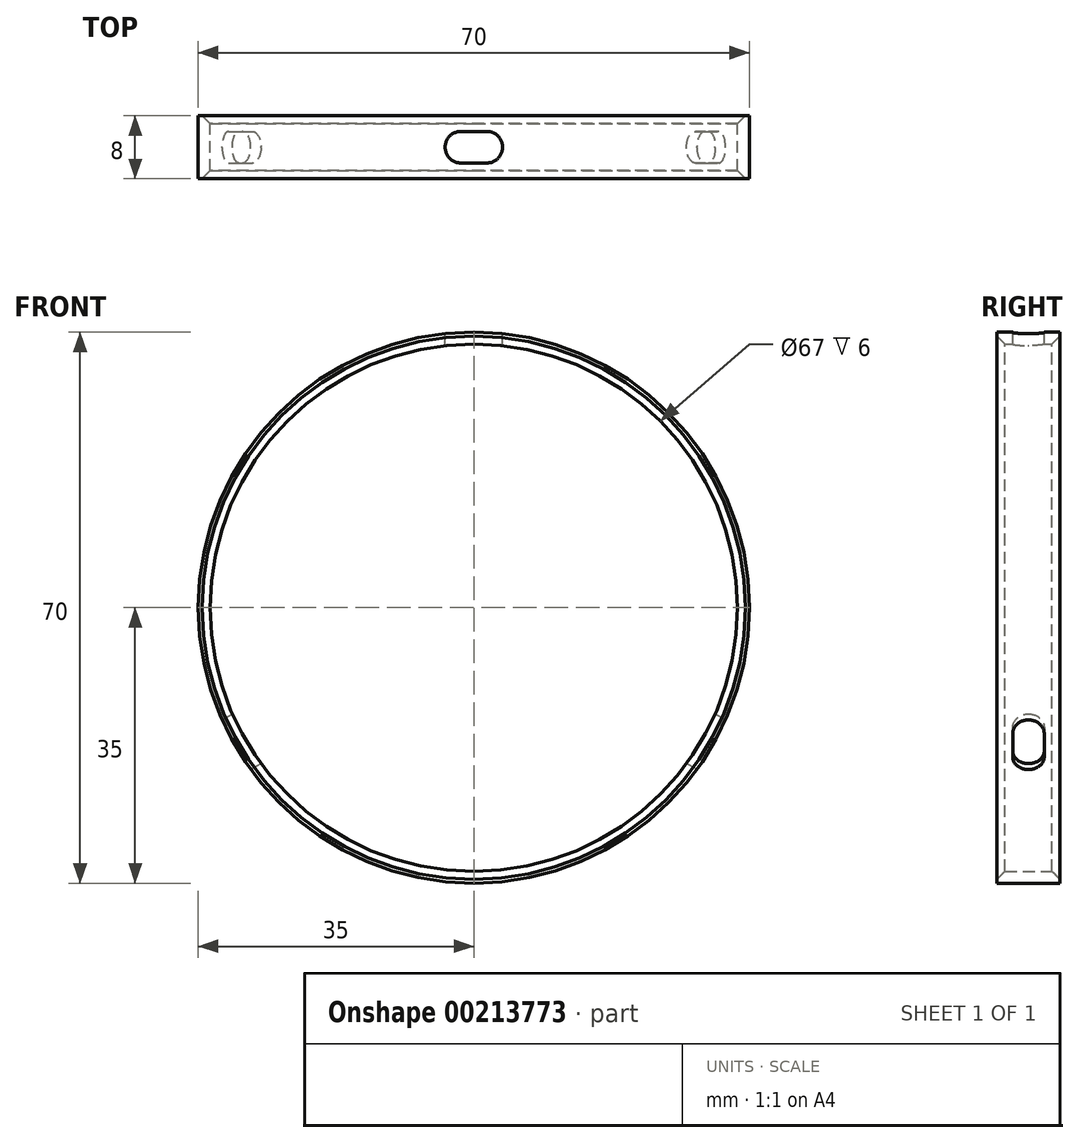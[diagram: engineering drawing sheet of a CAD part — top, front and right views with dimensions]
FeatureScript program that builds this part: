
annotation { "Feature Type Name" : "Feature", "Feature Type Description" : "" }
export const myFeature = defineFeature(function(context is Context, id is Id, definition is map)
    precondition{}
    {
        {
            var Q0;
            Q0=qCreatedBy(makeId("Front.planeOp"),FACE);
            var sketch = newSketch(context, id + "F0", { "sketchPlane" : qUnion([Q0])});
            skCircle(sketch, "E0", {"center": v(0, 0) * mm, "radius": 33.5 * mm});
            skCircle(sketch, "E1.0", {"center": v(0, 0) * mm, "radius": 35 * mm});
            skLineSegment(sketch, "E2.bottom", {"start": v(3.63, 34.81) * mm, "end": v(-3.63, 34.81) * mm, "construction": true});
            skLineSegment(sketch, "E2.top", {"start": v(3.63, 36.97) * mm, "end": v(-3.63, 36.97) * mm});
            skLineSegment(sketch, "E2.left", {"start": v(3.63, 34.81) * mm, "end": v(3.63, 36.97) * mm});
            skLineSegment(sketch, "E2.right", {"start": v(-3.63, 34.81) * mm, "end": v(-3.63, 36.97) * mm});
            skPoint(sketch, "E2.middle", {"position": v(0, 35.89) * mm});
            skLineSegment(sketch, "E3.1.0", {"start": v(-28.33, -20.55) * mm, "end": v(-30.2, -21.63) * mm});
            skLineSegment(sketch, "E3.1.1", {"start": v(-31.96, -14.26) * mm, "end": v(-33.83, -15.34) * mm});
            skLineSegment(sketch, "E3.1.2", {"start": v(-33.83, -15.34) * mm, "end": v(-30.2, -21.63) * mm});
            skLineSegment(sketch, "E3.1.3", {"start": v(-31.96, -14.26) * mm, "end": v(-28.33, -20.55) * mm, "construction": true});
            skLineSegment(sketch, "E3.2.0", {"start": v(31.96, -14.26) * mm, "end": v(33.83, -15.34) * mm});
            skLineSegment(sketch, "E3.2.1", {"start": v(28.33, -20.55) * mm, "end": v(30.2, -21.63) * mm});
            skLineSegment(sketch, "E3.2.2", {"start": v(30.2, -21.63) * mm, "end": v(33.83, -15.34) * mm});
            skLineSegment(sketch, "E3.2.3", {"start": v(28.33, -20.55) * mm, "end": v(31.96, -14.26) * mm, "construction": true});
            skLineSegment(sketch, "E4", {"start": v(0, 0) * mm, "end": v(24.75, 24.75) * mm, "construction": true});
            skLineSegment(sketch, "E5", {"start": v(0, 0) * mm, "end": v(-24.75, 24.75) * mm, "construction": true});
            skLineSegment(sketch, "E6.MirrorCS", {"start": v(0, 0) * mm, "end": v(24.75, -24.75) * mm, "construction": true});
            skLineSegment(sketch, "E7.MirrorCS", {"start": v(0, 0) * mm, "end": v(-24.75, -24.75) * mm, "construction": true});
            skLineSegment(sketch, "E8.0", {"start": v(-0.14, 0.14) * mm, "end": v(0, 0.28) * mm});
            skLineSegment(sketch, "E9.MirrorCS", {"start": v(0.14, -0.14) * mm, "end": v(0.28, 0) * mm});
            skLineSegment(sketch, "E10.MirrorCS", {"start": v(0.14, 0.14) * mm, "end": v(0, 0.28) * mm});
            skLineSegment(sketch, "E11.MirrorCS", {"start": v(-0.14, -0.14) * mm, "end": v(-0.28, 0) * mm});
            skLineSegment(sketch, "E12.MirrorCS", {"start": v(0.14, 0.14) * mm, "end": v(0.28, 0) * mm});
            skLineSegment(sketch, "E13.MirrorCS", {"start": v(-0.14, -0.14) * mm, "end": v(0, -0.28) * mm});
            skLineSegment(sketch, "E14.MirrorCS", {"start": v(0.14, -0.14) * mm, "end": v(0, -0.28) * mm});
            skLineSegment(sketch, "E15.MirrorCS", {"start": v(-0.14, 0.14) * mm, "end": v(-0.28, 0) * mm});
            skLineSegment(sketch, "E16.trimOffspring", {"start": v(-7.2, -7.48) * mm, "end": v(-23.55, -23.83) * mm, "construction": true});
            skLineSegment(sketch, "E17.trimOffspring", {"start": v(-7.48, -7.2) * mm, "end": v(-23.83, -23.55) * mm, "construction": true});
            skLineSegment(sketch, "E18.trimOffspring", {"start": v(-7.48, 7.2) * mm, "end": v(-23.83, 23.55) * mm, "construction": true});
            skLineSegment(sketch, "E19.trimOffspring", {"start": v(-7.2, 7.48) * mm, "end": v(-23.55, 23.83) * mm, "construction": true});
            skLineSegment(sketch, "E20.trimOffspring", {"start": v(7.2, 7.48) * mm, "end": v(23.55, 23.83) * mm, "construction": true});
            skLineSegment(sketch, "E21.trimOffspring", {"start": v(7.48, 7.2) * mm, "end": v(23.83, 23.55) * mm, "construction": true});
            skLineSegment(sketch, "E22.trimOffspring", {"start": v(7.2, -7.48) * mm, "end": v(23.55, -23.83) * mm, "construction": true});
            skLineSegment(sketch, "E23.trimOffspring", {"start": v(7.48, -7.2) * mm, "end": v(23.83, -23.55) * mm, "construction": true});
            skLineSegment(sketch, "E24", {"start": v(-3.63, 34.81) * mm, "end": v(-3.63, 31.7) * mm});
            skLineSegment(sketch, "E25", {"start": v(-3.63, 31.7) * mm, "end": v(3.63, 31.7) * mm});
            skLineSegment(sketch, "E26", {"start": v(3.63, 31.7) * mm, "end": v(3.63, 34.81) * mm});
            skLineSegment(sketch, "E27", {"start": v(31.96, -14.26) * mm, "end": v(7.27, 0) * mm});
            skLineSegment(sketch, "E28", {"start": v(28.33, -20.55) * mm, "end": v(3.35, -6.13) * mm});
            skLineSegment(sketch, "E29", {"start": v(3.35, -6.13) * mm, "end": v(7.27, 0) * mm});
            skLineSegment(sketch, "E30", {"start": v(-28.33, -20.55) * mm, "end": v(-3.28, -6.1) * mm});
            skLineSegment(sketch, "E31", {"start": v(-31.96, -14.26) * mm, "end": v(-6.86, 0.24) * mm});
            skLineSegment(sketch, "E32", {"start": v(-6.86, 0.24) * mm, "end": v(-3.28, -6.1) * mm});
            skLineSegment(sketch, "E33", {"start": v(0, -0.28) * mm, "end": v(0, 35) * mm, "construction": true});
            skLineSegment(sketch, "E34", {"start": v(0.28, 0) * mm, "end": v(-20.96, 28.03) * mm});
            skLineSegment(sketch, "E35.MirrorCS", {"start": v(-0.28, 0) * mm, "end": v(20.96, 28.03) * mm});
            skSolve(sketch);
        }
        {
            var Q0;
            Q0=makeQuery(id+"F0.imprint","IMPRINT",FACE,{"disambiguationData":[TD([[makeQuery(id+"F0.imprint","IMPRINT",EDGE,{"derivedFrom":sQuery(id+"F0.wireOp",EDGE,"E0")}),-1.0]])]});
            var Q1;
            {var subQ2=sQuery(id+"F0.wireOp",EDGE,"E16.trimOffspring");var subQ7=sQuery(id+"F0.wireOp",EDGE,"E0");var subQ9=makeQuery(id+"F0.imprint","INTERSECT",VERTEX,{"derivedFrom":[subQ7,subQ2]});Q1=makeQuery(id+"F0.imprint","IMPRINT",FACE,{"disambiguationData":[TD([[makeQuery(id+"F0.imprint","IMPRINT",EDGE,{"disambiguationData":[TD([[subQ9,-1.0]])],"derivedFrom":subQ7}),-1.0]])]});}
            var Q2;
            {var subQ5=sQuery(id+"F0.wireOp",EDGE,"E21.trimOffspring");var subQ7=sQuery(id+"F0.wireOp",EDGE,"E0");var subQ8=makeQuery(id+"F0.imprint","INTERSECT",VERTEX,{"derivedFrom":[subQ7,subQ5]});Q2=makeQuery(id+"F0.imprint","IMPRINT",FACE,{"disambiguationData":[TD([[makeQuery(id+"F0.imprint","IMPRINT",EDGE,{"disambiguationData":[TD([[subQ8,1.0]])],"derivedFrom":subQ7}),-1.0]])]});}
            var Q3;
            {var subQ2=sQuery(id+"F0.wireOp",EDGE,"E19.trimOffspring");var subQ7=sQuery(id+"F0.wireOp",EDGE,"E0");var subQ8=makeQuery(id+"F0.imprint","INTERSECT",VERTEX,{"derivedFrom":[subQ7,subQ2]});Q3=makeQuery(id+"F0.imprint","IMPRINT",FACE,{"disambiguationData":[TD([[makeQuery(id+"F0.imprint","IMPRINT",EDGE,{"disambiguationData":[TD([[subQ8,1.0]])],"derivedFrom":subQ7}),-1.0]])]});}
            var Q4;
            {var subQ5=sQuery(id+"F0.wireOp",EDGE,"E17.trimOffspring");var subQ6=sQuery(id+"F0.wireOp",EDGE,"E0");var subQ7=makeQuery(id+"F0.imprint","INTERSECT",VERTEX,{"derivedFrom":[subQ6,subQ5]});Q4=makeQuery(id+"F0.imprint","IMPRINT",FACE,{"disambiguationData":[TD([[makeQuery(id+"F0.imprint","IMPRINT",EDGE,{"disambiguationData":[TD([[subQ7,1.0]])],"derivedFrom":subQ6}),-1.0]])]});}
            extrude(context, id + "F1", {"entities" : qUnion([Q0, Q1, Q2, Q3, Q4]), "depth" : 4 * mm, "hasSecondDirection" : true, "secondDirectionOppositeDirection" : true, "secondDirectionDepth" : 4 * mm});
        }
        {
            var Q0;
            Q0=makeQuery(id+"F1.opExtrude","CAP_EDGE",EDGE,{"disambiguationData":[OSD([sQuery(id+"F0.wireOp",EDGE,"E0")])],"isStart":false});
            var Q1;
            Q1=makeQuery(id+"F1.opExtrude","CAP_EDGE",EDGE,{"disambiguationData":[OSD([sQuery(id+"F0.wireOp",EDGE,"E0")])],"isStart":true});
            chamfer(context, id + "F2", {"entities" : qUnion([Q0, Q1]), "width" : 1 * mm, "tangentPropagation" : true});
        }
        {
            var Q0;
            Q0=qCreatedBy(makeId("Top.planeOp"),FACE);
            var sketch = newSketch(context, id + "F3", { "sketchPlane" : qUnion([Q0])});
            skCircle(sketch, "E36", {"center": v(0, 0) * mm, "radius": 0.15 * mm});
            skCircle(sketch, "E37.1.0.0", {"center": v(0, -0.6) * mm, "radius": 0.15 * mm});
            skCircle(sketch, "E37.2.0.0", {"center": v(0, -1.2) * mm, "radius": 0.15 * mm});
            skCircle(sketch, "E37.3.0.0", {"center": v(0, -1.8) * mm, "radius": 0.15 * mm});
            skCircle(sketch, "E37.4.0.0", {"center": v(0, -2.4) * mm, "radius": 0.15 * mm});
            skCircle(sketch, "E37.5.0.0", {"center": v(0, -3) * mm, "radius": 0.15 * mm});
            skCircle(sketch, "E37.6.0.0", {"center": v(0, -3.6) * mm, "radius": 0.15 * mm});
            skLineSegment(sketch, "E37.direction1", {"start": v(0, 0) * mm, "end": v(0, -0.6) * mm, "construction": true});
            skCircle(sketch, "E38.MirrorC", {"center": v(0, 0.6) * mm, "radius": 0.15 * mm});
            skCircle(sketch, "E39.MirrorC", {"center": v(0, 1.2) * mm, "radius": 0.15 * mm});
            skCircle(sketch, "E40.MirrorC", {"center": v(0, 1.8) * mm, "radius": 0.15 * mm});
            skCircle(sketch, "E41.MirrorC", {"center": v(0, 2.4) * mm, "radius": 0.15 * mm});
            skCircle(sketch, "E42.MirrorC", {"center": v(0, 3) * mm, "radius": 0.15 * mm});
            skCircle(sketch, "E43.MirrorC", {"center": v(0, 3.6) * mm, "radius": 0.15 * mm});
            skSolve(sketch);
        }
        {
            var Q0;
            Q0=makeQuery(id+"F0.imprint","IMPRINT",FACE,{"disambiguationData":[TD([[makeQuery(id+"F0.imprint","IMPRINT",EDGE,{"derivedFrom":sQuery(id+"F0.wireOp",EDGE,"E2.top")}),1.0]])]});
            var Q1;
            {var subQ0=sQuery(id+"F0.wireOp",EDGE,"E24");var subQ1=sQuery(id+"F0.wireOp",EDGE,"E0");var subQ2=makeQuery(id+"F0.imprint","INTERSECT",VERTEX,{"derivedFrom":[subQ1,subQ0]});Q1=makeQuery(id+"F0.imprint","IMPRINT",FACE,{"disambiguationData":[TD([[makeQuery(id+"F0.imprint","IMPRINT",EDGE,{"disambiguationData":[TD([[subQ2,1.0]])],"derivedFrom":subQ1}),-1.0]])]});}
            var Q2;
            {var subQ5=sQuery(id+"F0.wireOp",EDGE,"E25");Q2=makeQuery(id+"F0.imprint","IMPRINT",FACE,{"disambiguationData":[TD([[makeQuery(id+"F0.imprint","IMPRINT",EDGE,{"derivedFrom":subQ5}),1.0]])]});}
            var Q3;
            {var subQ5=sQuery(id+"F0.wireOp",EDGE,"E29");Q3=makeQuery(id+"F0.imprint","IMPRINT",FACE,{"disambiguationData":[TD([[makeQuery(id+"F0.imprint","IMPRINT",EDGE,{"derivedFrom":subQ5}),-1.0]])]});}
            var Q4;
            {var subQ0=sQuery(id+"F0.wireOp",EDGE,"E28");var subQ1=sQuery(id+"F0.wireOp",EDGE,"E0");var subQ2=makeQuery(id+"F0.imprint","INTERSECT",VERTEX,{"derivedFrom":[subQ1,subQ0]});Q4=makeQuery(id+"F0.imprint","IMPRINT",FACE,{"disambiguationData":[TD([[makeQuery(id+"F0.imprint","IMPRINT",EDGE,{"disambiguationData":[TD([[subQ2,-1.0]])],"derivedFrom":subQ1}),-1.0]])]});}
            var Q5;
            {var subQ0=sQuery(id+"F0.wireOp",EDGE,"E3.2.0");Q5=makeQuery(id+"F0.imprint","IMPRINT",FACE,{"disambiguationData":[TD([[makeQuery(id+"F0.imprint","IMPRINT",EDGE,{"derivedFrom":subQ0}),-1.0]])]});}
            var Q6;
            {var subQ5=sQuery(id+"F0.wireOp",EDGE,"E32");Q6=makeQuery(id+"F0.imprint","IMPRINT",FACE,{"disambiguationData":[TD([[makeQuery(id+"F0.imprint","IMPRINT",EDGE,{"derivedFrom":subQ5}),-1.0]])]});}
            var Q7;
            {var subQ0=sQuery(id+"F0.wireOp",EDGE,"E3.1.0");Q7=makeQuery(id+"F0.imprint","IMPRINT",FACE,{"disambiguationData":[TD([[makeQuery(id+"F0.imprint","IMPRINT",EDGE,{"derivedFrom":subQ0}),-1.0]])]});}
            var Q8;
            {var subQ0=sQuery(id+"F0.wireOp",EDGE,"E31");var subQ1=sQuery(id+"F0.wireOp",EDGE,"E0");var subQ2=makeQuery(id+"F0.imprint","INTERSECT",VERTEX,{"derivedFrom":[subQ1,subQ0]});Q8=makeQuery(id+"F0.imprint","IMPRINT",FACE,{"disambiguationData":[TD([[makeQuery(id+"F0.imprint","IMPRINT",EDGE,{"disambiguationData":[TD([[subQ2,-1.0]])],"derivedFrom":subQ1}),-1.0]])]});}
            extrude(context, id + "F4", {"entities" : qUnion([Q0, Q1, Q2, Q3, Q4, Q5, Q6, Q7, Q8]), "operationType" : NewBodyOperationType.REMOVE, "oppositeDirection" : true, "depth" : 2 * mm, "hasSecondDirection" : true, "secondDirectionOppositeDirection" : false, "secondDirectionDepth" : 2 * mm});
        }
        {
            var Q0;
            Q0=makeQuery(id+"F4.boolean.opBoolean","COPY",EDGE,{"derivedFrom":makeQuery(id+"F4.opExtrude","CAP_EDGE",EDGE,{"disambiguationData":[OSD([sQuery(id+"F0.wireOp",EDGE,"E3.2.1"),sQuery(id+"F0.wireOp",EDGE,"E28")])],"isStart":false})});
            var Q1;
            Q1=makeQuery(id+"F4.boolean.opBoolean","COPY",EDGE,{"derivedFrom":makeQuery(id+"F4.opExtrude","CAP_EDGE",EDGE,{"disambiguationData":[OSD([sQuery(id+"F0.wireOp",EDGE,"E3.2.0"),sQuery(id+"F0.wireOp",EDGE,"E27")])],"isStart":false})});
            var Q2;
            Q2=makeQuery(id+"F4.boolean.opBoolean","COPY",EDGE,{"derivedFrom":makeQuery(id+"F4.opExtrude","CAP_EDGE",EDGE,{"disambiguationData":[OSD([sQuery(id+"F0.wireOp",EDGE,"E3.2.0"),sQuery(id+"F0.wireOp",EDGE,"E27")])],"isStart":true})});
            var Q3;
            Q3=makeQuery(id+"F4.boolean.opBoolean","COPY",EDGE,{"derivedFrom":makeQuery(id+"F4.opExtrude","CAP_EDGE",EDGE,{"disambiguationData":[OSD([sQuery(id+"F0.wireOp",EDGE,"E3.2.1"),sQuery(id+"F0.wireOp",EDGE,"E28")])],"isStart":true})});
            var Q4;
            Q4=makeQuery(id+"F4.boolean.opBoolean","COPY",EDGE,{"derivedFrom":makeQuery(id+"F4.opExtrude","CAP_EDGE",EDGE,{"disambiguationData":[OSD([sQuery(id+"F0.wireOp",EDGE,"E3.1.0"),sQuery(id+"F0.wireOp",EDGE,"E30")])],"isStart":false})});
            var Q5;
            Q5=makeQuery(id+"F4.boolean.opBoolean","COPY",EDGE,{"derivedFrom":makeQuery(id+"F4.opExtrude","CAP_EDGE",EDGE,{"disambiguationData":[OSD([sQuery(id+"F0.wireOp",EDGE,"E3.1.1"),sQuery(id+"F0.wireOp",EDGE,"E31")])],"isStart":false})});
            var Q6;
            Q6=makeQuery(id+"F4.boolean.opBoolean","COPY",EDGE,{"derivedFrom":makeQuery(id+"F4.opExtrude","CAP_EDGE",EDGE,{"disambiguationData":[OSD([sQuery(id+"F0.wireOp",EDGE,"E3.1.1"),sQuery(id+"F0.wireOp",EDGE,"E31")])],"isStart":true})});
            var Q7;
            Q7=makeQuery(id+"F4.boolean.opBoolean","COPY",EDGE,{"derivedFrom":makeQuery(id+"F4.opExtrude","CAP_EDGE",EDGE,{"disambiguationData":[OSD([sQuery(id+"F0.wireOp",EDGE,"E3.1.0"),sQuery(id+"F0.wireOp",EDGE,"E30")])],"isStart":true})});
            var Q8;
            Q8=makeQuery(id+"F4.boolean.opBoolean","COPY",EDGE,{"derivedFrom":makeQuery(id+"F4.opExtrude","CAP_EDGE",EDGE,{"disambiguationData":[OSD([sQuery(id+"F0.wireOp",EDGE,"E2.right"),sQuery(id+"F0.wireOp",EDGE,"E24")])],"isStart":false})});
            var Q9;
            Q9=makeQuery(id+"F4.boolean.opBoolean","COPY",EDGE,{"derivedFrom":makeQuery(id+"F4.opExtrude","CAP_EDGE",EDGE,{"disambiguationData":[OSD([sQuery(id+"F0.wireOp",EDGE,"E2.left"),sQuery(id+"F0.wireOp",EDGE,"E26")])],"isStart":false})});
            var Q10;
            Q10=makeQuery(id+"F4.boolean.opBoolean","COPY",EDGE,{"derivedFrom":makeQuery(id+"F4.opExtrude","CAP_EDGE",EDGE,{"disambiguationData":[OSD([sQuery(id+"F0.wireOp",EDGE,"E2.right"),sQuery(id+"F0.wireOp",EDGE,"E24")])],"isStart":true})});
            var Q11;
            Q11=makeQuery(id+"F4.boolean.opBoolean","COPY",EDGE,{"derivedFrom":makeQuery(id+"F4.opExtrude","CAP_EDGE",EDGE,{"disambiguationData":[OSD([sQuery(id+"F0.wireOp",EDGE,"E2.left"),sQuery(id+"F0.wireOp",EDGE,"E26")])],"isStart":true})});
            fillet(context, id + "F5", {"entities" : qUnion([Q0, Q1, Q2, Q3, Q4, Q5, Q6, Q7, Q8, Q9, Q10, Q11]), "radius" : 1.94 * mm, "tangentPropagation" : true, "allowEdgeOverflow" : false});
        }
    });
